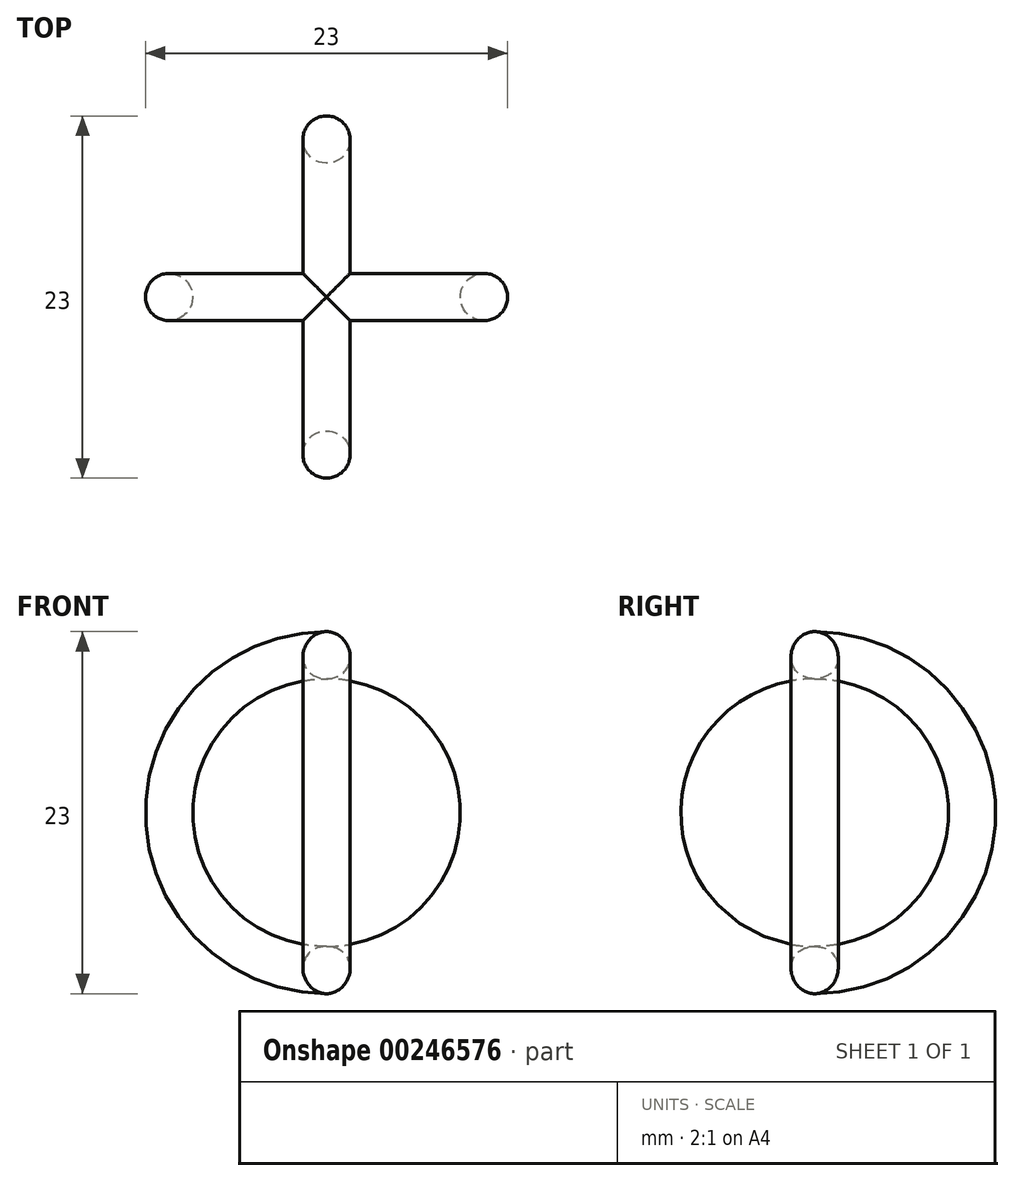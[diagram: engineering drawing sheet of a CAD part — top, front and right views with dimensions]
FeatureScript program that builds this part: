
annotation { "Feature Type Name" : "Feature", "Feature Type Description" : "" }
export const myFeature = defineFeature(function(context is Context, id is Id, definition is map)
    precondition{}
    {
        {
            var Q0;
            Q0=qCreatedBy(makeId("Top.planeOp"),FACE);
            var sketch = newSketch(context, id + "F0", { "sketchPlane" : qUnion([Q0])});
            skLineSegment(sketch, "E0", {"start": v(0, 0) * mm, "end": v(10, 0) * mm, "construction": true});
            skLineSegment(sketch, "E1", {"start": v(0, 0) * mm, "end": v(0, 10) * mm, "construction": true});
            skCircle(sketch, "E2", {"center": v(0, 10) * mm, "radius": 1.5 * mm});
            skCircle(sketch, "E3", {"center": v(10, 0) * mm, "radius": 1.5 * mm});
            skSolve(sketch);
        }
        {
            var Q0;
            Q0=makeQuery(id+"F0.imprint","IMPRINT",FACE,{"disambiguationData":[TD([[makeQuery(id+"F0.imprint","IMPRINT",EDGE,{"derivedFrom":sQuery(id+"F0.wireOp",EDGE,"E3")}),1.0]])]});
            var Q1;
            Q1=sQuery(id+"F0.wireOp",EDGE,"E2");
            var Q2;
            Q2=sQuery(id+"F0.wireOp",EDGE,"E3");
            var Q3;
            Q3=sQuery(id+"F0.wireOp",EDGE,"E1");
            revolve(context, id + "F1", {"entities" : qUnion([Q0]), "surfaceEntities" : qUnion([Q1, Q2]), "axis" : qUnion([Q3]), "revolveType" : RevolveType.FULL});
        }
        {
            var Q0;
            Q0=makeQuery(id+"F0.imprint","IMPRINT",FACE,{"disambiguationData":[TD([[makeQuery(id+"F0.imprint","IMPRINT",EDGE,{"derivedFrom":sQuery(id+"F0.wireOp",EDGE,"E3")}),1.0]])]});
            var Q1;
            Q1=sQuery(id+"F0.wireOp",EDGE,"E3");
            var Q2;
            Q2=sQuery(id+"F0.wireOp",EDGE,"E2");
            var Q3;
            Q3=sQuery(id+"F0.wireOp",EDGE,"E1");
            revolve(context, id + "F2", {"operationType" : NewBodyOperationType.ADD, "entities" : qUnion([Q0]), "surfaceEntities" : qUnion([Q1, Q2]), "axis" : qUnion([Q3]), "revolveType" : RevolveType.FULL});
        }
        {
            var Q0;
            Q0=makeQuery(id+"F0.imprint","IMPRINT",FACE,{"disambiguationData":[TD([[makeQuery(id+"F0.imprint","IMPRINT",EDGE,{"derivedFrom":sQuery(id+"F0.wireOp",EDGE,"E2")}),1.0]])]});
            var Q1;
            Q1=sQuery(id+"F0.wireOp",EDGE,"E2");
            var Q2;
            Q2=sQuery(id+"F0.wireOp",EDGE,"E0");
            revolve(context, id + "F3", {"operationType" : NewBodyOperationType.ADD, "entities" : qUnion([Q0]), "surfaceEntities" : qUnion([Q1]), "axis" : qUnion([Q2]), "revolveType" : RevolveType.FULL});
        }
    });
